# Revit family: Terra 42 - Ground Light
name_source: partatom
category: Lighting Fixtures
revit_build: Autodesk Revit 2018 (Build: 20170223_1515(x64)
units: mm (PartAtom-declared; Revit-internal decimal feet)

## family parameters
Always vertical = Yes
Cut with Voids When Loaded = No
Host = Ceiling
Light Source = Yes
OmniClass Number = 23.80.70.11
OmniClass Title = Luminaries for Internal Lighting
Part Type = Normal
Room Calculation Point = No
Round Connector Dimension = Use Diameter
Shared = No

## types (2) — shared parameters
Color Filter = 16777215
Dimming Lamp Color Temperature Shift = <None>
Light Source Symbol Length = 3048 mm  [stored 10 ft]
Spot Field Angle = 90.00°

## per-type parameters (varying)
| type | Apparent Load | Dimmable | Dimming Method | Driver Included | Driver Required | Efficacy (lm/w) | Electrical Class | Lamp | Light Source Fixed | Location Rating | Main Finish | Main Material | Power (Watts) | Product Code | Product Location | Product Name | Product SKU | Spot Beam Angle | Tilt Angle |
| CE | 4 VA | Yes | Control Gear Dependent | No | Constant Current 700mA | 37.86 | 3 | LED | Yes | IP67 | Annodised Aluminium | Aluminium | 2.6 | 0936 | Outdoor | Terra 42 | 1201002 | 25.00° | -90.00° |
| ETL | 0 VA |  |  |  |  |  |  |  |  |  |  |  |  |  |  |  |  | 30.00° | 60.00° |

note: [stored X ft] marks values corroborated as IEEE doubles in the binary element streams (Revit-internal decimal feet)

## geometry (parser evidence)
native form markers: Sweep x2
no freeform markers — native parametric forms only
